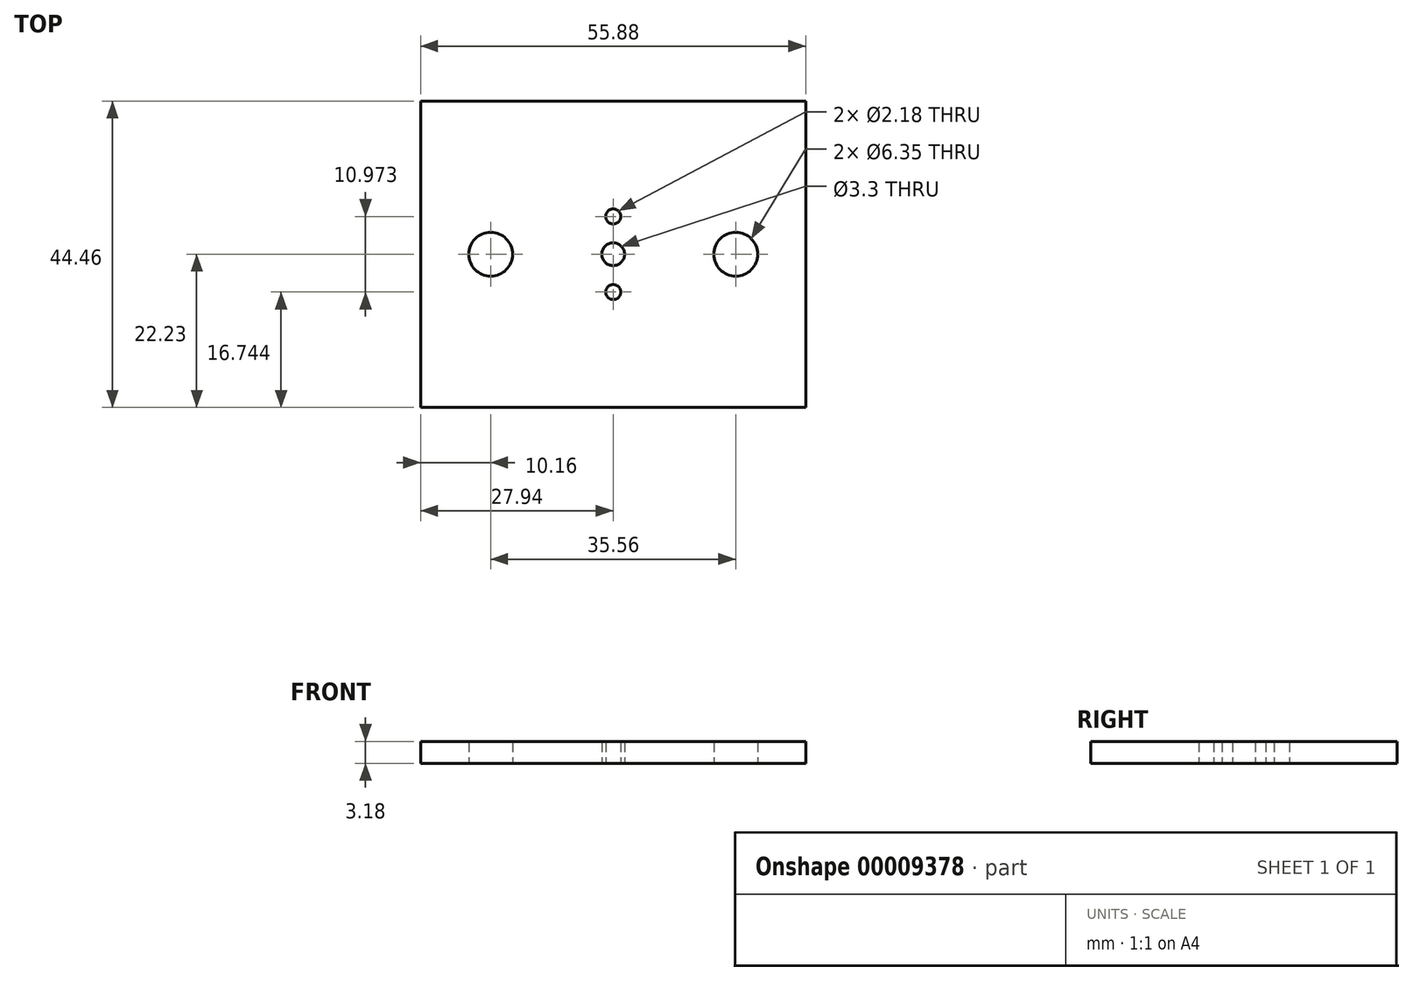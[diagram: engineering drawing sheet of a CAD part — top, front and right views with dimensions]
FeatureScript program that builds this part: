
annotation { "Feature Type Name" : "Feature", "Feature Type Description" : "" }
export const myFeature = defineFeature(function(context is Context, id is Id, definition is map)
    precondition{}
    {
        {
            var Q0;
            Q0=qCreatedBy(makeId("Top.planeOp"),FACE);
            var sketch = newSketch(context, id + "F0", { "sketchPlane" : qUnion([Q0])});
            skLineSegment(sketch, "E0.rect.bottom", {"start": v(27.94, 22.22) * mm, "end": v(-27.94, 22.23) * mm});
            skLineSegment(sketch, "E0.rect.top", {"start": v(27.94, -22.23) * mm, "end": v(-27.94, -22.22) * mm});
            skLineSegment(sketch, "E0.rect.left", {"start": v(27.94, 22.23) * mm, "end": v(27.94, -22.23) * mm});
            skLineSegment(sketch, "E0.rect.right", {"start": v(-27.94, 22.23) * mm, "end": v(-27.94, -22.22) * mm});
            skPoint(sketch, "E0.rect.middle", {"position": v(0, 0) * mm});
            skCircle(sketch, "E1", {"center": v(0, 0) * mm, "radius": 1.65 * mm});
            skCircle(sketch, "E2", {"center": v(-17.78, 0) * mm, "radius": 3.18 * mm});
            skCircle(sketch, "E3", {"center": v(17.78, 0) * mm, "radius": 3.18 * mm});
            skCircle(sketch, "E4", {"center": v(0, 5.49) * mm, "radius": 1.1 * mm});
            skCircle(sketch, "E5", {"center": v(0, -5.49) * mm, "radius": 1.1 * mm});
            skSolve(sketch);
        }
        {
            var Q0;
            Q0=makeQuery(id+"F0.imprint","IMPRINT",FACE,{"disambiguationData":[TD([[makeQuery(id+"F0.imprint","IMPRINT",EDGE,{"derivedFrom":sQuery(id+"F0.wireOp",EDGE,"E0.rect.bottom")}),1.0]])]});
            extrude(context, id + "F1", {"entities" : qUnion([Q0]), "depth" : 3.17 * mm});
        }
    });
